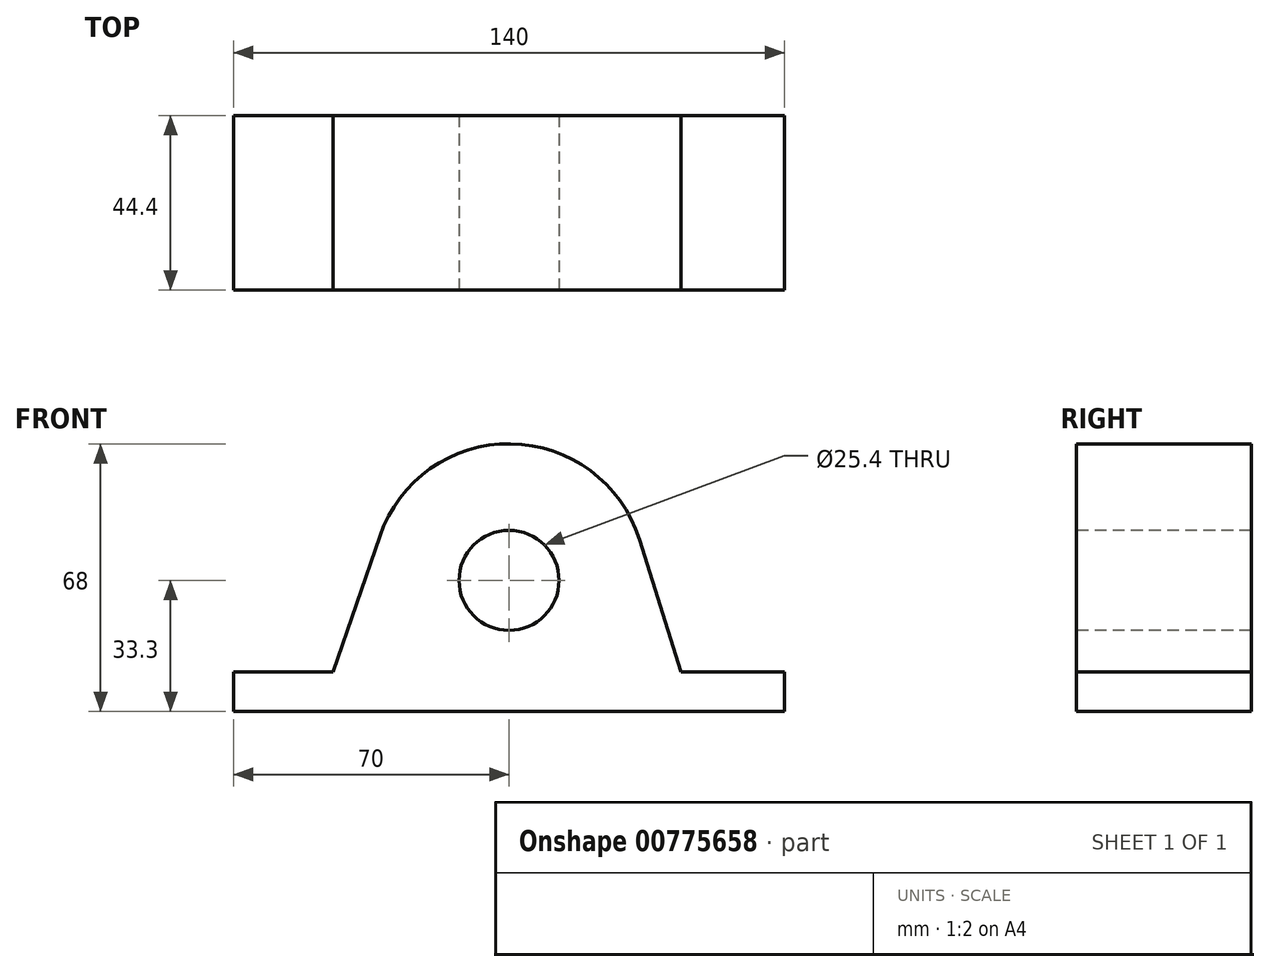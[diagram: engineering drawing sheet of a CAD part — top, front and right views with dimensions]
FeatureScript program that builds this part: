
annotation { "Feature Type Name" : "Feature", "Feature Type Description" : "" }
export const myFeature = defineFeature(function(context is Context, id is Id, definition is map)
    precondition{}
    {
        {
            var Q0;
            Q0=qCreatedBy(makeId("Front.planeOp"),FACE);
            var sketch = newSketch(context, id + "F0", { "sketchPlane" : qUnion([Q0])});
            skCircle(sketch, "E0", {"center": v(0, 0) * mm, "radius": 12.7 * mm});
            skLineSegment(sketch, "E1.bottom", {"start": v(-70, -33.3) * mm, "end": v(70, -33.3) * mm});
            skLineSegment(sketch, "E1.top", {"start": v(-70, -23.3) * mm, "end": v(70, -23.3) * mm});
            skLineSegment(sketch, "E1.left", {"start": v(-70, -33.3) * mm, "end": v(-70, -23.3) * mm});
            skLineSegment(sketch, "E1.right", {"start": v(70, -33.3) * mm, "end": v(70, -23.3) * mm});
            skArc(sketch, "E2", {"start": v(33.1, 10.44) * mm, "mid": v(0.42, 34.7) * mm, "end": v(-32.83, 11.24) * mm});
            skLineSegment(sketch, "E3", {"start": v(43.74, -23.3) * mm, "end": v(33.1, 10.44) * mm});
            skLineSegment(sketch, "E4", {"start": v(-44.66, -23.3) * mm, "end": v(-32.83, 11.24) * mm});
            skSolve(sketch);
        }
        {
            var Q0;
            Q0=makeQuery(id+"F0.imprint","IMPRINT",FACE,{"disambiguationData":[TD([[makeQuery(id+"F0.imprint","IMPRINT",EDGE,{"derivedFrom":sQuery(id+"F0.wireOp",EDGE,"E0")}),-1.0]])]});
            var Q1;
            Q1=makeQuery(id+"F0.imprint","IMPRINT",FACE,{"disambiguationData":[TD([[makeQuery(id+"F0.imprint","IMPRINT",EDGE,{"derivedFrom":sQuery(id+"F0.wireOp",EDGE,"E1.bottom")}),1.0]])]});
            extrude(context, id + "F1", {"entities" : qUnion([Q0, Q1]), "oppositeDirection" : true, "depth" : 44.4 * mm, "offsetDistance" : 25 * mm, "symmetric" : true});
        }
    });
